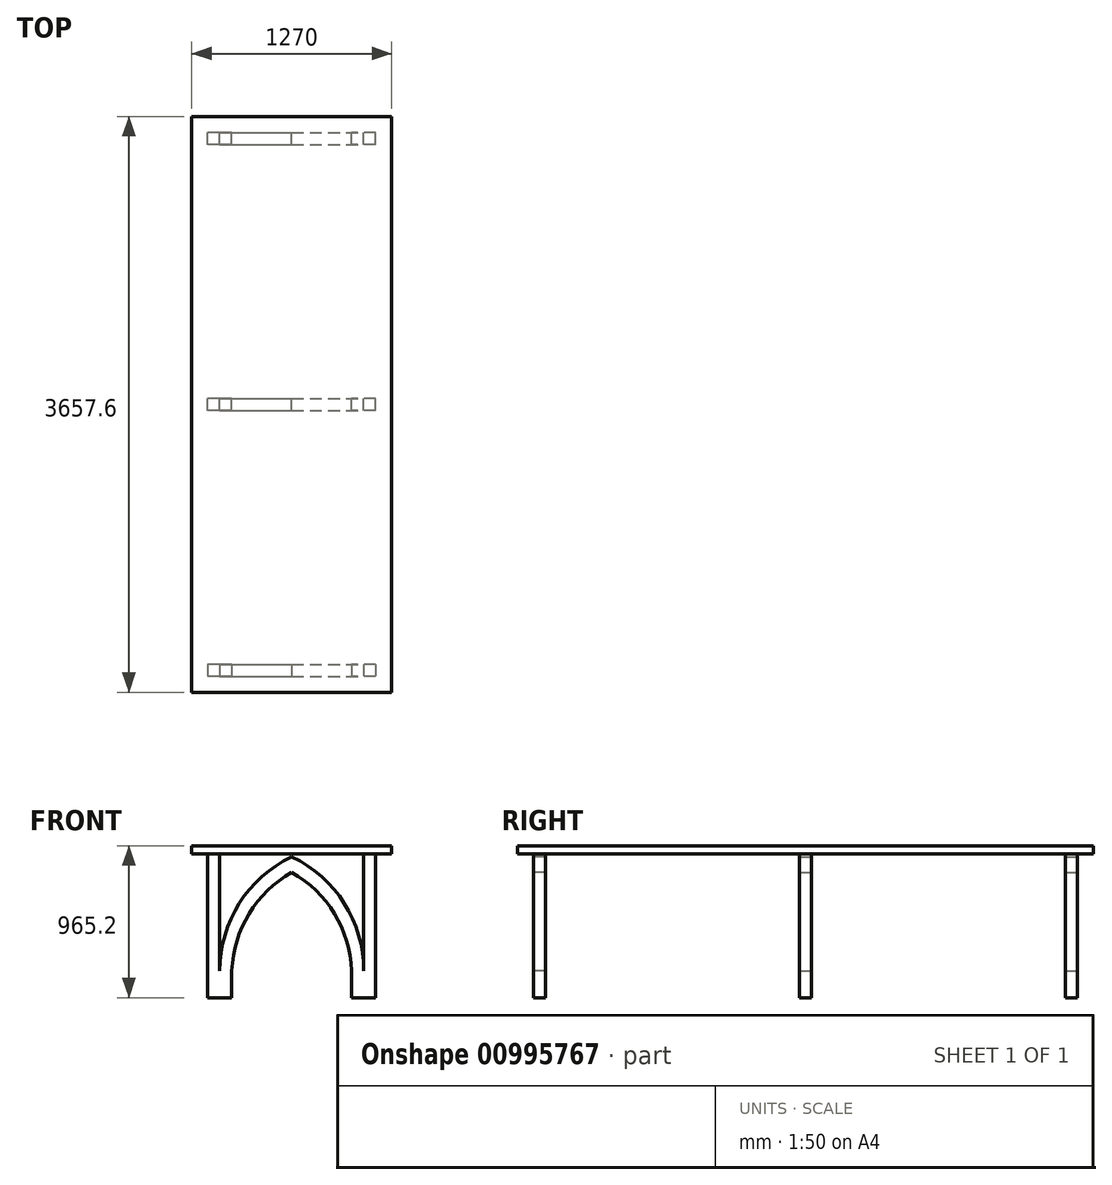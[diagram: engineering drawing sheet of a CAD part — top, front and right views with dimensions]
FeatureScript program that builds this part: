
annotation { "Feature Type Name" : "Feature", "Feature Type Description" : "" }
export const myFeature = defineFeature(function(context is Context, id is Id, definition is map)
    precondition{}
    {
        {
            var Q0;
            Q0=qCreatedBy(makeId("Right.planeOp"),FACE);
            var sketch = newSketch(context, id + "F0", { "sketchPlane" : qUnion([Q0])});
            skLineSegment(sketch, "E0.bottom", {"start": v(-1828.8, 0) * mm, "end": v(1828.8, 0) * mm, "construction": true});
            skLineSegment(sketch, "E0.top", {"start": v(-1828.8, -914.4) * mm, "end": v(1828.8, -914.4) * mm, "construction": true});
            skLineSegment(sketch, "E0.left", {"start": v(-1828.8, 0) * mm, "end": v(-1828.8, -914.4) * mm, "construction": true});
            skLineSegment(sketch, "E0.right", {"start": v(1828.8, 0) * mm, "end": v(1828.8, -914.4) * mm, "construction": true});
            skPoint(sketch, "E0.middle", {"position": v(0, -457.2) * mm});
            skLineSegment(sketch, "E1", {"start": v(-1727.2, 0) * mm, "end": v(-1727.2, 101.6) * mm});
            skSolve(sketch);
        }
        {
            var Q0;
            Q0=sQuery(id+"F0.wireOp",EDGE,"E1");
            cPlane(context, id + "F1", {"entities" : qUnion([Q0]), "cplaneType" : CPlaneType.LINE_ANGLE, "offset" : 25.4 * mm, "angle" : 90 * degree, "width" : 152.4 * mm, "height" : 152.4 * mm});
        }
        {
            var Q0;
            Q0=qCreatedBy(id+"F1.planeOp",FACE);
            var sketch = newSketch(context, id + "F2", { "sketchPlane" : qUnion([Q0])});
            skLineSegment(sketch, "E2.bottom", {"start": v(0, 0) * mm, "end": v(76.2, 0) * mm});
            skLineSegment(sketch, "E2.top", {"start": v(0, -914.4) * mm, "end": v(76.2, -914.4) * mm});
            skLineSegment(sketch, "E2.left", {"start": v(0, 0) * mm, "end": v(0, -914.4) * mm});
            skLineSegment(sketch, "E2.right", {"start": v(76.2, 0) * mm, "end": v(76.2, -914.4) * mm});
            skLineSegment(sketch, "E3.bottom", {"start": v(990.6, 0) * mm, "end": v(1066.8, 0) * mm});
            skLineSegment(sketch, "E3.top", {"start": v(990.6, -914.4) * mm, "end": v(1066.8, -914.4) * mm});
            skLineSegment(sketch, "E3.left", {"start": v(990.6, 0) * mm, "end": v(990.6, -914.4) * mm});
            skLineSegment(sketch, "E3.right", {"start": v(1066.8, 0) * mm, "end": v(1066.8, -914.4) * mm});
            skArc(sketch, "E4", {"start": v(990.6, -742.6) * mm, "mid": v(866.7, -315.26) * mm, "end": v(533.4, -20.48) * mm});
            skLineSegment(sketch, "E5", {"start": v(990.6, -20.48) * mm, "end": v(76.2, -20.48) * mm, "construction": true});
            skLineSegment(sketch, "E6", {"start": v(533.4, -20.48) * mm, "end": v(533.4, -290.67) * mm, "construction": true});
            skArc(sketch, "E7", {"start": v(914.4, -742.6) * mm, "mid": v(804.55, -381.36) * mm, "end": v(533.4, -118.6) * mm});
            skLineSegment(sketch, "E8", {"start": v(533.4, -118.6) * mm, "end": v(576.6, -42.56) * mm, "construction": true});
            skLineSegment(sketch, "E9", {"start": v(804.55, -381.36) * mm, "end": v(879.24, -335.76) * mm, "construction": true});
            skLineSegment(sketch, "E10", {"start": v(804.55, -381.36) * mm, "end": v(790.63, -358.56) * mm, "construction": true});
            skPoint(sketch, "E10.endSnap0", {"position": v(841.9, -358.56) * mm});
            skLineSegment(sketch, "E11", {"start": v(533.4, -118.6) * mm, "end": v(494.04, -96.22) * mm, "construction": true});
            skLineSegment(sketch, "E12", {"start": v(914.4, -742.6) * mm, "end": v(914.4, -914.4) * mm});
            skLineSegment(sketch, "E13", {"start": v(914.4, -742.6) * mm, "end": v(990.6, -742.6) * mm, "construction": true});
            skLineSegment(sketch, "E14", {"start": v(914.4, -914.4) * mm, "end": v(990.6, -914.4) * mm});
            skLineSegment(sketch, "E15.MirrorCS", {"start": v(152.4, -742.6) * mm, "end": v(152.4, -914.4) * mm});
            skLineSegment(sketch, "E16.MirrorCS", {"start": v(152.4, -914.4) * mm, "end": v(76.2, -914.4) * mm});
            skArc(sketch, "E17.MirrorCS", {"start": v(76.2, -742.6) * mm, "mid": v(200.1, -315.26) * mm, "end": v(533.4, -20.48) * mm});
            skArc(sketch, "E18.MirrorCS", {"start": v(152.4, -742.6) * mm, "mid": v(262.25, -381.36) * mm, "end": v(533.4, -118.6) * mm});
            skSolve(sketch);
        }
        {
            var Q0;
            Q0 = qSketchRegion(id + "F2", true);
            extrude(context, id + "F3", {"entities" : qUnion([Q0]), "depth" : 76.2 * mm, "offsetDistance" : 25.4 * mm});
        }
        {
            var Q0;
            Q0=qCreatedBy(makeId("Right.planeOp"),FACE);
            var sketch = newSketch(context, id + "F4", { "sketchPlane" : qUnion([Q0])});
            skLineSegment(sketch, "E19", {"start": v(0, 0) * mm, "end": v(-1689.1, 0) * mm, "construction": true});
            skSolve(sketch);
        }
        {
            var Q0;
            Q0=sQuery(id+"F4.wireOp",EDGE,"E19");
            cPlane(context, id + "F5", {"entities" : qUnion([Q0]), "cplaneType" : CPlaneType.MID_PLANE, "offset" : 25.4 * mm, "width" : 152.4 * mm, "height" : 152.4 * mm});
        }
        {
            var Q0;
            Q0=makeQuery(id+"F3.opExtrude","SWEPT_BODY",BODY,{"disambiguationData":[OSD([sQuery(id+"F2.wireOp",EDGE,"E2.bottom"),sQuery(id+"F2.wireOp",EDGE,"E2.top"),sQuery(id+"F2.wireOp",EDGE,"E2.left"),sQuery(id+"F2.wireOp",EDGE,"E2.right"),sQuery(id+"F2.wireOp",EDGE,"E3.bottom"),sQuery(id+"F2.wireOp",EDGE,"E3.top"),sQuery(id+"F2.wireOp",EDGE,"E3.left"),sQuery(id+"F2.wireOp",EDGE,"E3.right"),sQuery(id+"F2.wireOp",EDGE,"E4"),sQuery(id+"F2.wireOp",EDGE,"E7"),sQuery(id+"F2.wireOp",EDGE,"E12"),sQuery(id+"F2.wireOp",EDGE,"E14"),sQuery(id+"F2.wireOp",EDGE,"E15.MirrorCS"),sQuery(id+"F2.wireOp",EDGE,"E16.MirrorCS"),sQuery(id+"F2.wireOp",EDGE,"E17.MirrorCS"),sQuery(id+"F2.wireOp",EDGE,"E18.MirrorCS")])]});
            var Q1;
            Q1=qCreatedBy(id+"F5.planeOp",FACE);
            mirror(context, id + "F6", {"entities" : qUnion([Q0]), "mirrorPlane" : qUnion([Q1])});
        }
        {
            var Q0;
            Q0=makeQuery(id+"F3.opExtrude","SWEPT_BODY",BODY,{"disambiguationData":[OSD([sQuery(id+"F2.wireOp",EDGE,"E2.bottom"),sQuery(id+"F2.wireOp",EDGE,"E2.top"),sQuery(id+"F2.wireOp",EDGE,"E2.left"),sQuery(id+"F2.wireOp",EDGE,"E2.right"),sQuery(id+"F2.wireOp",EDGE,"E3.bottom"),sQuery(id+"F2.wireOp",EDGE,"E3.top"),sQuery(id+"F2.wireOp",EDGE,"E3.left"),sQuery(id+"F2.wireOp",EDGE,"E3.right"),sQuery(id+"F2.wireOp",EDGE,"E4"),sQuery(id+"F2.wireOp",EDGE,"E7"),sQuery(id+"F2.wireOp",EDGE,"E12"),sQuery(id+"F2.wireOp",EDGE,"E14"),sQuery(id+"F2.wireOp",EDGE,"E15.MirrorCS"),sQuery(id+"F2.wireOp",EDGE,"E16.MirrorCS"),sQuery(id+"F2.wireOp",EDGE,"E17.MirrorCS"),sQuery(id+"F2.wireOp",EDGE,"E18.MirrorCS")])]});
            var Q1;
            Q1=qCreatedBy(makeId("Front.planeOp"),FACE);
            mirror(context, id + "F7", {"entities" : qUnion([Q0]), "mirrorPlane" : qUnion([Q1])});
        }
        {
            var Q0;
            Q0=qCreatedBy(makeId("Top.planeOp"),FACE);
            var sketch = newSketch(context, id + "F8", { "sketchPlane" : qUnion([Q0])});
            skLineSegment(sketch, "E20.bottom", {"start": v(-1168.4, 1828.8) * mm, "end": v(101.6, 1828.8) * mm});
            skLineSegment(sketch, "E20.top", {"start": v(-1168.4, -1828.8) * mm, "end": v(101.6, -1828.8) * mm});
            skLineSegment(sketch, "E20.left", {"start": v(-1168.4, 1828.8) * mm, "end": v(-1168.4, -1828.8) * mm});
            skLineSegment(sketch, "E20.right", {"start": v(101.6, 1828.8) * mm, "end": v(101.6, -1828.8) * mm});
            skPoint(sketch, "E20.middle", {"position": v(-533.4, 0) * mm});
            skSolve(sketch);
        }
        {
            var Q0;
            Q0 = qSketchRegion(id + "F8", true);
            extrude(context, id + "F9", {"entities" : qUnion([Q0]), "depth" : 50.8 * mm, "offsetDistance" : 25.4 * mm});
        }
    });
